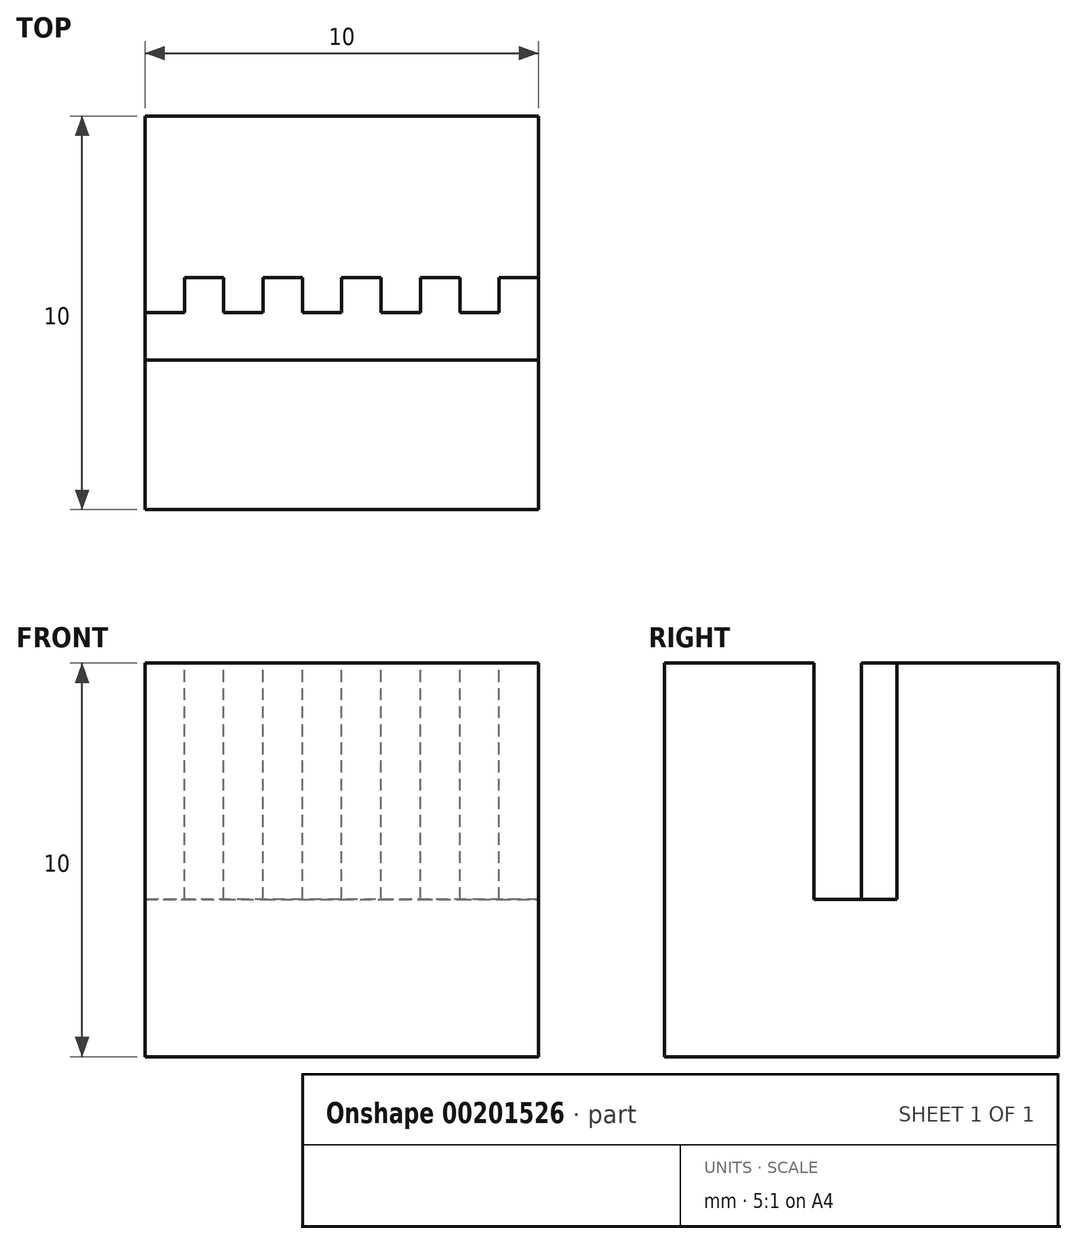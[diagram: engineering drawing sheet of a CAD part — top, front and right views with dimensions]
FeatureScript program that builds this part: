
annotation { "Feature Type Name" : "Feature", "Feature Type Description" : "" }
export const myFeature = defineFeature(function(context is Context, id is Id, definition is map)
    precondition{}
    {
        {
            var Q0;
            Q0=qCreatedBy(makeId("Top.planeOp"),FACE);
            var sketch = newSketch(context, id + "F0", { "sketchPlane" : qUnion([Q0])});
            skLineSegment(sketch, "E0.bottom", {"start": v(-5, 5) * mm, "end": v(5, 5) * mm});
            skLineSegment(sketch, "E0.top", {"start": v(-5, -5) * mm, "end": v(5, -5) * mm});
            skLineSegment(sketch, "E0.left", {"start": v(-5, 5) * mm, "end": v(-5, -5) * mm});
            skLineSegment(sketch, "E0.right", {"start": v(5, 5) * mm, "end": v(5, -5) * mm});
            skPoint(sketch, "E0.middle", {"position": v(0, 0) * mm});
            skSolve(sketch);
        }
        {
            var Q0;
            Q0=makeQuery(id+"F0.imprint","IMPRINT",FACE,{"disambiguationData":[TD([[makeQuery(id+"F0.imprint","IMPRINT",EDGE,{"derivedFrom":sQuery(id+"F0.wireOp",EDGE,"E0.bottom")}),-1.0]])]});
            extrude(context, id + "F1", {"entities" : qUnion([Q0]), "depth" : 10 * mm});
        }
        {
            var Q0;
            Q0=makeQuery(id+"F1.opExtrude","CAP_FACE",FACE,{"disambiguationData":[OSD([sQuery(id+"F0.wireOp",EDGE,"E0.bottom"),sQuery(id+"F0.wireOp",EDGE,"E0.top"),sQuery(id+"F0.wireOp",EDGE,"E0.left"),sQuery(id+"F0.wireOp",EDGE,"E0.right")])],"isStart":false});
            var sketch = newSketch(context, id + "F2", { "sketchPlane" : qUnion([Q0])});
            skLineSegment(sketch, "E1", {"start": v(-5, 0.9) * mm, "end": v(-5, 0) * mm});
            skLineSegment(sketch, "E2", {"start": v(-5, 0) * mm, "end": v(-4, 0) * mm});
            skLineSegment(sketch, "E3", {"start": v(-4, 0) * mm, "end": v(-4, 0.9) * mm});
            skLineSegment(sketch, "E4", {"start": v(-4, 0.9) * mm, "end": v(-3, 0.9) * mm});
            skLineSegment(sketch, "E5.1.0.0", {"start": v(-2, 0.9) * mm, "end": v(-1, 0.9) * mm});
            skLineSegment(sketch, "E5.1.0.1", {"start": v(-2, 0) * mm, "end": v(-2, 0.9) * mm});
            skLineSegment(sketch, "E5.1.0.2", {"start": v(-3, 0) * mm, "end": v(-2, 0) * mm});
            skLineSegment(sketch, "E5.1.0.3", {"start": v(-3, 0.9) * mm, "end": v(-3, 0) * mm});
            skLineSegment(sketch, "E5.2.0.0", {"start": v(0, 0.9) * mm, "end": v(1, 0.9) * mm});
            skLineSegment(sketch, "E5.2.0.1", {"start": v(0, 0) * mm, "end": v(0, 0.9) * mm});
            skLineSegment(sketch, "E5.2.0.2", {"start": v(-1, 0) * mm, "end": v(0, 0) * mm});
            skLineSegment(sketch, "E5.2.0.3", {"start": v(-1, 0.9) * mm, "end": v(-1, 0) * mm});
            skLineSegment(sketch, "E5.direction1", {"start": v(-5, 0) * mm, "end": v(-3, 0) * mm, "construction": true});
            skLineSegment(sketch, "E6.0.3.0", {"start": v(2, 0.9) * mm, "end": v(3, 0.9) * mm});
            skLineSegment(sketch, "E6.3.3.0", {"start": v(2, 0) * mm, "end": v(2, 0.9) * mm});
            skLineSegment(sketch, "E6.6.3.0", {"start": v(1, 0) * mm, "end": v(2, 0) * mm});
            skLineSegment(sketch, "E6.9.3.0", {"start": v(1, 0.9) * mm, "end": v(1, 0) * mm});
            skLineSegment(sketch, "E6.0.4.0", {"start": v(4, 0.9) * mm, "end": v(5, 0.9) * mm});
            skLineSegment(sketch, "E6.3.4.0", {"start": v(4, 0) * mm, "end": v(4, 0.9) * mm});
            skLineSegment(sketch, "E6.6.4.0", {"start": v(3, 0) * mm, "end": v(4, 0) * mm});
            skLineSegment(sketch, "E6.9.4.0", {"start": v(3, 0.9) * mm, "end": v(3, 0) * mm});
            skLineSegment(sketch, "E7", {"start": v(5, 0) * mm, "end": v(5, -1.2) * mm});
            skLineSegment(sketch, "E8", {"start": v(5, -1.2) * mm, "end": v(-5, -1.2) * mm});
            skSolve(sketch);
        }
        {
            var Q0;
            {var subQ0=sQuery(id+"F2.wireOp",EDGE,"E2");Q0=makeQuery(id+"F2.imprint","IMPRINT",FACE,{"disambiguationData":[TD([[makeQuery(id+"F2.imprint","IMPRINT",EDGE,{"derivedFrom":subQ0}),-1.0]])]});}
            extrude(context, id + "F3", {"entities" : qUnion([Q0]), "operationType" : NewBodyOperationType.REMOVE, "oppositeDirection" : true, "depth" : 6 * mm});
        }
    });
